FCSTD DOCUMENT  (FreeCAD 0.19R24291 (Git))
Label: magn_coil03
License: All rights reserved
LicenseURL: http://en.wikipedia.org/wiki/All_rights_reserved
objects: Part::Sweep×2, Spreadsheet::Sheet×1, Sketcher::SketchObject×1, PartDesign::Pad×1, PartDesign::Body×1, Part::Box×1, Part::Fillet×1, Part::Helix×1, Part::Line×1, Part::MultiCommon×1, Part::Circle×1, Part::FeaturePython×1
note: 13 computed .brp shape members not serialized (recipe doc carries the construction recipe); baked Part::Feature solids carry a one-line shape summary decoded from their .brp

FEATURE [Spreadsheet::Sheet] Spreadsheet
  cells = C2=in; D2=out; E2=blank; B3=coil ln; C3(coil_ln)=7.5; F3(bln_ln)=7; B4=coil w; C4(coil_w)=10.2; D4(coil_w1)=10.6; F4(bln_w)=10.7; B5=coil h; C5(coil_h)=1.2; D5(coil_h1)=1.6; F5(bln_h)=1.7; B6=coil th; C6(coil_th)=0.2; F6=0.3; B7=coil g; C7(coil_g)=0.1; F7=13.6; B8=coil b; C8(coil_b)=0.2; D8(coil_b1)=0.25; F8=1; B9=wire r; C9(wire_r)=0.5; F9=1; B10=wire n ; C10(wire_n)=60
FEATURE [Sketcher::SketchObject] Sketch
  FullyConstrained = true
  MapMode = 5
  Support = -> [XY_Plane]
  expr: Constraints[51] = Spreadsheet.coil_b
  expr: Constraints[50] = Spreadsheet.coil_b
  expr: Constraints[49] = Spreadsheet.coil_b
  expr: Constraints[47] = Spreadsheet.coil_b1
  expr: Constraints[46] = Spreadsheet.coil_b
  expr: Constraints[53] = Spreadsheet.coil_b1
  expr: Constraints[11] = Spreadsheet.coil_h1
  expr: Constraints[52] = Spreadsheet.coil_b1
  expr: Constraints[48] = Spreadsheet.coil_b1
  expr: Constraints[8] = Spreadsheet.coil_w
  expr: Constraints[10] = Spreadsheet.coil_h
  expr: Constraints[9] = Spreadsheet.coil_w1
  sketch-geometry (24):
    g0: LineSegment StartX=-4.9 StartY=0.6 StartZ=0 EndX=4.9 EndY=0.6 EndZ=0
    g1: LineSegment StartX=5.1 StartY=0.4 StartZ=0 EndX=5.1 EndY=-0.4 EndZ=0
    g2: LineSegment StartX=4.9 StartY=-0.6 StartZ=0 EndX=-4.9 EndY=-0.6 EndZ=0
    g3: LineSegment StartX=-5.1 StartY=-0.4 StartZ=0 EndX=-5.1 EndY=0.4 EndZ=0
    g4: LineSegment StartX=-5.05 StartY=0.8 StartZ=0 EndX=5.05 EndY=0.8 EndZ=0
    g5: LineSegment StartX=5.3 StartY=0.55 StartZ=0 EndX=5.3 EndY=-0.55 EndZ=0
    g6: LineSegment StartX=5.05 StartY=-0.8 StartZ=0 EndX=-5.05 EndY=-0.8 EndZ=0
    g7: LineSegment StartX=-5.3 StartY=-0.55 StartZ=0 EndX=-5.3 EndY=0.55 EndZ=0
    g8: ArcOfCircle CenterX=-5.05 CenterY=0.55 CenterZ=0 NormalX=0 NormalY=0 NormalZ=1 AngleXU=0 Radius=0.25 StartAngle=1.5708 EndAngle=3.14159
    g9: GeomPoint X=-5.3 Y=0.8 Z=0
    g10: ArcOfCircle CenterX=-5.05 CenterY=-0.55 CenterZ=0 NormalX=0 NormalY=0 NormalZ=1 AngleXU=0 Radius=0.25 StartAngle=3.14159 EndAngle=4.71239
    g11: GeomPoint X=-5.3 Y=-0.8 Z=0
    g12: ArcOfCircle CenterX=-4.9 CenterY=0.4 CenterZ=0 NormalX=0 NormalY=0 NormalZ=1 AngleXU=0 Radius=0.2 StartAngle=1.5708 EndAngle=3.14159
    g13: GeomPoint X=-5.1 Y=0.6 Z=0
    g14: ArcOfCircle CenterX=-4.9 CenterY=-0.4 CenterZ=0 NormalX=0 NormalY=0 NormalZ=1 AngleXU=0 Radius=0.2 StartAngle=3.14159 EndAngle=4.71239
    g15: GeomPoint X=-5.1 Y=-0.6 Z=0
    g16: ArcOfCircle CenterX=5.05 CenterY=0.55 CenterZ=0 NormalX=0 NormalY=0 NormalZ=1 AngleXU=0 Radius=0.25 StartAngle=0 EndAngle=1.5708
    g17: GeomPoint X=5.3 Y=0.8 Z=0
    g18: ArcOfCircle CenterX=4.9 CenterY=0.4 CenterZ=0 NormalX=0 NormalY=0 NormalZ=1 AngleXU=0 Radius=0.2 StartAngle=0 EndAngle=1.5708
    g19: GeomPoint X=5.1 Y=0.6 Z=0
    g20: ArcOfCircle CenterX=5.05 CenterY=-0.55 CenterZ=0 NormalX=0 NormalY=0 NormalZ=1 AngleXU=0 Radius=0.25 StartAngle=4.71239 EndAngle=6.28319
    g21: GeomPoint X=5.3 Y=-0.8 Z=0
    g22: ArcOfCircle CenterX=4.9 CenterY=-0.4 CenterZ=0 NormalX=0 NormalY=0 NormalZ=1 AngleXU=0 Radius=0.2 StartAngle=4.71239 EndAngle=6.28319
    g23: GeomPoint X=5.1 Y=-0.6 Z=0
  constraints (54):
    c: Horizontal(g0)
    c: Horizontal(g2)
    c: Vertical(g1)
    c: Vertical(g3)
    c: Horizontal(g4)
    c: Horizontal(g6)
    c: Vertical(g5)
    c: Vertical(g7)
    c: DistanceX(g13,g19) = 10.2
    c: DistanceX(g9,g17) = 10.6
    c: DistanceY(g23,g19) = 1.2
    c: DistanceY(g21,g17) = 1.6
    c: Symmetric(g17,g11,g-1)
    c: Symmetric(g23,g13,g-1)
    c: PointOnObject(g9,g4)
    c: PointOnObject(g9,g7)
    c: Tangent(g4,g8) = 1.5708
    c: Tangent(g7,g8) = 1.5708
    c: PointOnObject(g11,g6)
    c: PointOnObject(g11,g7)
    c: Tangent(g6,g10) = 1.5708
    c: Tangent(g7,g10) = 1.5708
    c: PointOnObject(g13,g0)
    c: PointOnObject(g13,g3)
    c: Tangent(g0,g12) = 1.5708
    c: Tangent(g3,g12) = 1.5708
    c: PointOnObject(g15,g2)
    c: PointOnObject(g15,g3)
    c: Tangent(g2,g14) = 1.5708
    c: Tangent(g3,g14) = 1.5708
    c: PointOnObject(g17,g4)
    c: PointOnObject(g17,g5)
    c: Tangent(g4,g16) = 1.5708
    c: Tangent(g5,g16) = 1.5708
    c: PointOnObject(g19,g0)
    c: PointOnObject(g19,g1)
    c: Tangent(g0,g18) = 1.5708
    c: Tangent(g1,g18) = 1.5708
    c: PointOnObject(g21,g5)
    c: PointOnObject(g21,g6)
    c: Tangent(g5,g20) = 1.5708
    c: Tangent(g6,g20) = 1.5708
    c: PointOnObject(g23,g1)
    c: PointOnObject(g23,g2)
    c: Tangent(g1,g22) = 1.5708
    c: Tangent(g2,g22) = 1.5708
    c: Radius(g18) = 0.2
    c: Radius(g16) = 0.25
    c: Radius(g20) = 0.25
    c: Radius(g22) = 0.2
    c: Radius(g12) = 0.2
    c: Radius(g14) = 0.2
    c: Radius(g10) = 0.25
    c: Radius(g8) = 0.25
FEATURE [PartDesign::Pad] Pad
  Direction = (1,1,1)
  Length = 7.5
  Length2 = 100
  Profile = -> Sketch
  Type = 0
  expr: Length = Spreadsheet.coil_ln
FEATURE [PartDesign::Body] Body
  Group = -> [Sketch,Pad]
  Origin = -> Origin
  Placement = pos=(-0.45,0.05,-0.3) rot=(0,0,1;0rad)
  Tip = -> Pad
FEATURE [Part::Box] Box  label="Cube"
  AttacherType = Attacher::AttachEngine3D
  Height = 7
  Length = 10.7
  Placement = pos=(-5.8,-1.3,0.3) rot=(0,0,1;0rad)
  Width = 1.7
  expr: Length = Spreadsheet.bln_w
  expr: Width = Spreadsheet.bln_h
  expr: Height = Spreadsheet.bln_ln
FEATURE [Part::Fillet] Fillet
  Base = -> Box
  Edges = 4 edges r=0.3: [Edge1,Edge3,Edge5,Edge7]
  Placement = pos=(0,0.5,-1) rot=(0,0,1;0rad)
FEATURE [Part::Helix] Helix
  Angle = 0
  AttacherType = Attacher::AttachEngine3D
  Height = 0.1
  LocalCoord = 0
  Pitch = 0.1
  Radius = 7.4
  Style = 1
FEATURE [Part::Line] Line
  AttacherType = Attacher::AttachEngine3D
  X1 = 0
  X2 = 7.4
  Y1 = 0
  Y2 = 0
  Z1 = 0
  Z2 = 0
FEATURE [Part::Sweep] Sweep
  Frenet = true
  Sections = -> [Line]
  Solid = false
  Spine = -> Helix [Edge1]
  Transition = 1
FEATURE [Part::MultiCommon] Common
  Shapes = -> [Sweep,Fillet]
FEATURE [Part::Circle] Circle
  Angle0 = 0
  Angle1 = 360
  AttacherType = Attacher::AttachEngine3D
  Placement = pos=(4.9,0,0.1) rot=(1,0,0;1.5708rad)
  Radius = 0.05
FEATURE [Part::Sweep] Sweep001
  Frenet = false
  Sections = -> [Circle]
  Solid = true
  Spine = -> Common [Edge3,Edge4,Edge5,Edge6,Edge7,Edge8,Edge9,Edge10,Edge11]
  Transition = 1
FEATURE [Part::FeaturePython] Array  # Draft array (typed FeaturePython)
  Angle = 360
  ArrayType = 0
  Axis = (0,0,1)
  Base = -> Sweep001
  Center = (0,0,0)
  Count = 70
  ExpandArray = false
  Fuse = true
  IntervalAxis = (0,0,0)
  IntervalX = (100,0,0.1)
  IntervalY = (0,100,0.1)
  IntervalZ = (0,0,0.1)
  NumberCircles = 3
  NumberPolar = 5
  NumberX = 1
  NumberY = 1
  NumberZ = 70
  PlacementList = 70 placements: arithmetic series from (0,0,0) step (0,0,0.1) to (0,0,6.9)
  RadialDistance = 50
  ScaleList = (70) [(1,1,1),(1,1,1),(1,1,1),(1,1,1),(1,1,1),(1,1,1),(1,1,1),(1,1,1),(1,1,1),(1,1,1),(1,1,1),(1,1,1),(1,1,1),(1,1,1),(1,1,1),(1,1,1),(1,1,1),(1,1,1),+52 more]
  Symmetry = 1
  TangentialDistance = 25
